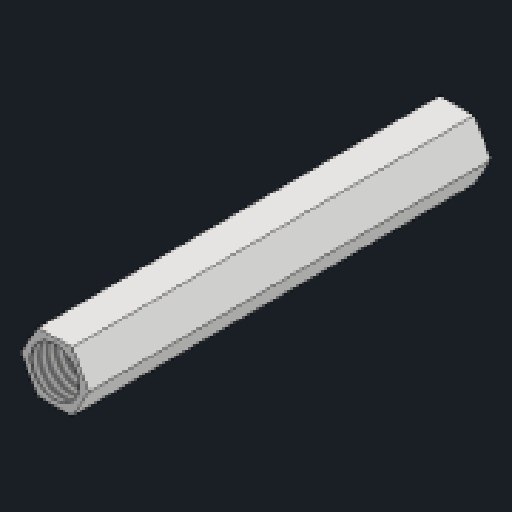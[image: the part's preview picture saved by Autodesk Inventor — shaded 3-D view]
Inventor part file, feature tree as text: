
AUTODESK INVENTOR PART (.ipt)
format: ipt  version: 2023.2 (Build 272271030, 271C)  size: 92,672 bytes
history: native  units: mm
features: extrude x1, thread x1, sketch x1
ambient origin geometry x8: Origin, YZ Plane, XZ Plane, XY Plane, X Axis, Y Axis, Z Axis, Center Point
bodies: Solid1 (feature_tree)
feature tree (3):
  extrude  "Extrusion1"  Depth=25.0mm TaperAngle=0.0deg
  thread  "Thread1"  [1 undecoded]
  sketch  "Sketch1"  dims[d0=3.7mm d1=25.0mm d2=0.0mm d3=3.0mm d4=25.0mm d5=0.0mm]
note: 1 required parameter value undecoded (feature->parameter linkage not recoverable at this tier; creation-order binding heuristic only, values carry confidence <= 0.55)
